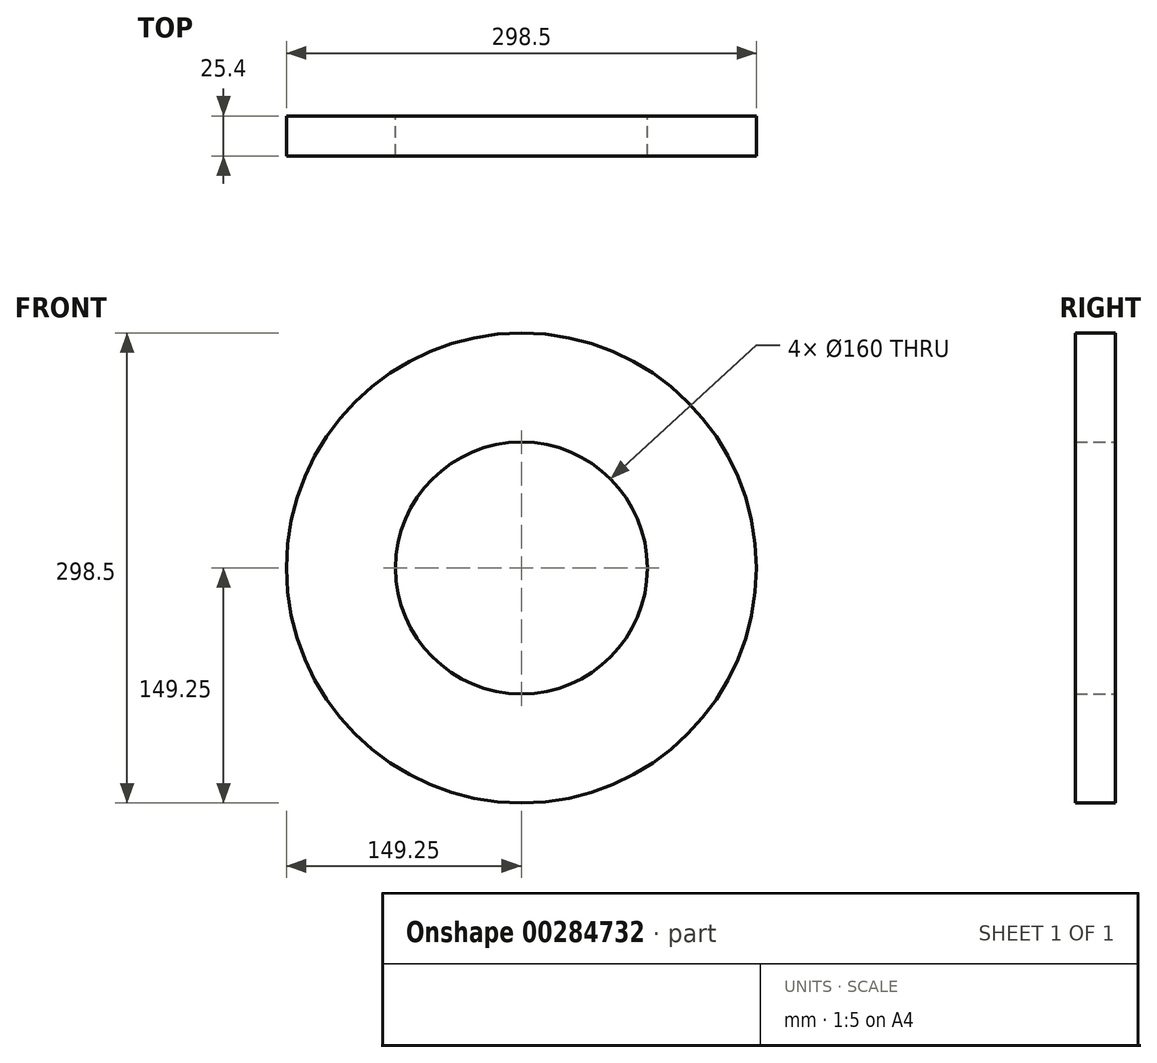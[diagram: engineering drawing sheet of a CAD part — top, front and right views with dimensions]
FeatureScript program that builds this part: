
annotation { "Feature Type Name" : "Feature", "Feature Type Description" : "" }
export const myFeature = defineFeature(function(context is Context, id is Id, definition is map)
    precondition{}
    {
        {
            var Q0;
            Q0=qCreatedBy(makeId("Front.planeOp"),FACE);
            var sketch = newSketch(context, id + "F0", { "sketchPlane" : qUnion([Q0])});
            skCircle(sketch, "E0", {"center": v(0, 0) * mm, "radius": 149.25 * mm});
            skCircle(sketch, "E1", {"center": v(0, 0) * mm, "radius": 80 * mm});
            skSolve(sketch);
        }
        {
            var Q0;
            Q0=qSketchRegion(id+"F0",true);
            extrude(context, id + "F1", {"entities" : qUnion([Q0]), "depth" : 25.4 * mm});
        }
    });
